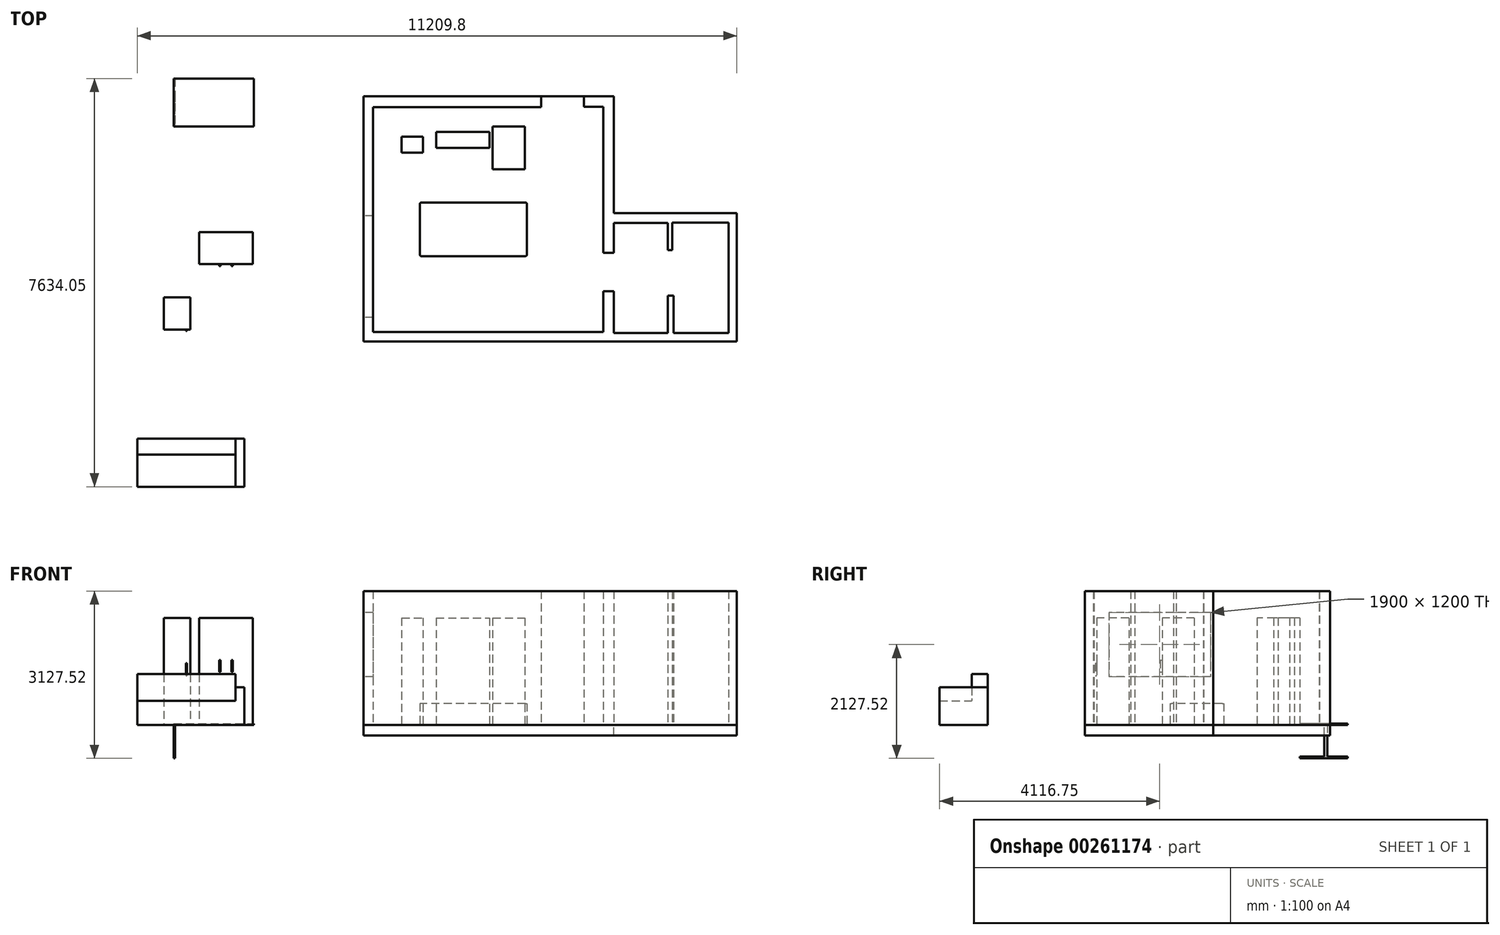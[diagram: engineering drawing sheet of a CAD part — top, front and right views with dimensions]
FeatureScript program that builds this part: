
annotation { "Feature Type Name" : "Feature", "Feature Type Description" : "" }
export const myFeature = defineFeature(function(context is Context, id is Id, definition is map)
    precondition{}
    {
        {
            var Q0;
            Q0=qCreatedBy(makeId("Top.planeOp"),FACE);
            var sketch = newSketch(context, id + "F0", { "sketchPlane" : qUnion([Q0])});
            skLineSegment(sketch, "E0", {"start": v(-190.9, 2081.06) * mm, "end": v(-3330.86, 2081.06) * mm});
            skLineSegment(sketch, "E1", {"start": v(-3330.86, 2081.06) * mm, "end": v(-3330.86, -2128.66) * mm});
            skLineSegment(sketch, "E2", {"start": v(-3330.86, -2128.66) * mm, "end": v(971.2, -2128.66) * mm});
            skLineSegment(sketch, "E3", {"start": v(971.2, -2128.66) * mm, "end": v(971.2, -1366.75) * mm});
            skLineSegment(sketch, "E4", {"start": v(971.2, -1366.75) * mm, "end": v(1171.3, -1366.75) * mm});
            skLineSegment(sketch, "E5", {"start": v(1171.3, -1366.75) * mm, "end": v(1171.3, -2144.05) * mm});
            skLineSegment(sketch, "E6", {"start": v(1171.3, -2144.05) * mm, "end": v(2179.48, -2144.05) * mm});
            skLineSegment(sketch, "E7", {"start": v(2179.48, -2144.05) * mm, "end": v(2179.48, -1443.71) * mm});
            skLineSegment(sketch, "E8", {"start": v(2179.48, -1443.71) * mm, "end": v(2287.22, -1443.71) * mm});
            skLineSegment(sketch, "E9", {"start": v(2287.22, -1443.71) * mm, "end": v(2287.22, -2144.05) * mm});
            skLineSegment(sketch, "E10", {"start": v(2287.22, -2144.05) * mm, "end": v(3318.49, -2144.05) * mm});
            skLineSegment(sketch, "E11", {"start": v(3318.49, -2144.05) * mm, "end": v(3318.49, -81.52) * mm});
            skLineSegment(sketch, "E12", {"start": v(3318.49, -81.52) * mm, "end": v(2264.13, -81.52) * mm});
            skLineSegment(sketch, "E13", {"start": v(2264.13, -81.52) * mm, "end": v(2264.13, -597.15) * mm});
            skLineSegment(sketch, "E14", {"start": v(2264.13, -597.15) * mm, "end": v(2179.48, -597.15) * mm});
            skLineSegment(sketch, "E15", {"start": v(2179.48, -597.15) * mm, "end": v(2179.48, -89.22) * mm});
            skLineSegment(sketch, "E16", {"start": v(2179.48, -89.22) * mm, "end": v(1171.3, -89.22) * mm});
            skLineSegment(sketch, "E17", {"start": v(1171.3, -89.22) * mm, "end": v(1171.3, -644.92) * mm});
            skLineSegment(sketch, "E18", {"start": v(1171.3, -644.92) * mm, "end": v(971.2, -644.92) * mm});
            skLineSegment(sketch, "E19", {"start": v(971.2, -644.92) * mm, "end": v(971.2, 2085.36) * mm});
            skLineSegment(sketch, "E20", {"start": v(971.2, 2085.36) * mm, "end": v(609.1, 2085.36) * mm});
            skLineSegment(sketch, "E21", {"start": v(609.1, 2085.36) * mm, "end": v(609.1, 2284.04) * mm});
            skLineSegment(sketch, "E22", {"start": v(609.1, 2284.04) * mm, "end": v(1171.3, 2284.04) * mm});
            skLineSegment(sketch, "E23", {"start": v(1171.3, 2284.04) * mm, "end": v(1171.3, 98.5) * mm});
            skLineSegment(sketch, "E24", {"start": v(1171.3, 98.5) * mm, "end": v(3468.44, 98.5) * mm});
            skLineSegment(sketch, "E25", {"start": v(3468.44, 98.5) * mm, "end": v(3468.44, -2303) * mm});
            skLineSegment(sketch, "E26", {"start": v(3468.44, -2303) * mm, "end": v(-3511.44, -2303) * mm});
            skLineSegment(sketch, "E27", {"start": v(-190.9, 2081.06) * mm, "end": v(-190.9, 2284.04) * mm});
            skLineSegment(sketch, "E28", {"start": v(-190.9, 2284.04) * mm, "end": v(-3511.44, 2284.04) * mm});
            skLineSegment(sketch, "E29", {"start": v(-3511.44, 2284.04) * mm, "end": v(-3511.44, -2303) * mm});
            skSolve(sketch);
        }
        {
            var Q0;
            Q0=qCreatedBy(makeId("Top.planeOp"),FACE);
            var sketch = newSketch(context, id + "F1", { "sketchPlane" : qUnion([Q0])});
            skLineSegment(sketch, "E30.bottom", {"start": v(-1094.62, 1714.75) * mm, "end": v(-494.62, 1714.75) * mm});
            skLineSegment(sketch, "E30.top", {"start": v(-1094.62, 914.75) * mm, "end": v(-494.62, 914.75) * mm});
            skLineSegment(sketch, "E30.left", {"start": v(-1094.62, 1714.75) * mm, "end": v(-1094.62, 914.75) * mm});
            skLineSegment(sketch, "E30.right", {"start": v(-494.62, 1714.75) * mm, "end": v(-494.62, 914.75) * mm});
            skSolve(sketch);
        }
        {
            var Q0;
            Q0 = qSketchRegion(id + "F0", true);
            extrude(context, id + "F2", {"entities" : qUnion([Q0]), "depth" : 2500 * mm});
        }
        {
            var Q0;
            Q0=makeQuery(id+"F2.opExtrude","SWEPT_FACE",FACE,{"disambiguationData":[OSD([sQuery(id+"F0.wireOp",EDGE,"E29")])]});
            var sketch = newSketch(context, id + "F3", { "sketchPlane" : qUnion([Q0])});
            skLineSegment(sketch, "E31.bottom", {"start": v(-47, 2100) * mm, "end": v(1853, 2100) * mm});
            skLineSegment(sketch, "E31.top", {"start": v(-47, 900) * mm, "end": v(1853, 900) * mm});
            skLineSegment(sketch, "E31.left", {"start": v(-47, 2100) * mm, "end": v(-47, 900) * mm});
            skLineSegment(sketch, "E31.right", {"start": v(1853, 2100) * mm, "end": v(1853, 900) * mm});
            skSolve(sketch);
        }
        {
            var Q0;
            Q0 = qSketchRegion(id + "F3", true);
            extrude(context, id + "F4", {"entities" : qUnion([Q0]), "operationType" : NewBodyOperationType.REMOVE, "endBound" : BoundingType.UP_TO_NEXT, "oppositeDirection" : true, "depth" : 25 * mm});
        }
        {
            var Q0;
            Q0=makeQuery(id+"F1.imprint","IMPRINT",FACE,{"disambiguationData":[TD([[makeQuery(id+"F1.imprint","IMPRINT",EDGE,{"derivedFrom":sQuery(id+"F1.wireOp",EDGE,"E30.bottom")}),-1.0]])]});
            extrude(context, id + "F5", {"entities" : qUnion([Q0]), "depth" : 2000 * mm});
        }
        {
            var Q0;
            Q0=qCreatedBy(makeId("Top.planeOp"),FACE);
            var sketch = newSketch(context, id + "F6", { "sketchPlane" : qUnion([Q0])});
            skLineSegment(sketch, "E32.bottom", {"start": v(-481.22, 293.15) * mm, "end": v(-2431.22, 293.15) * mm});
            skLineSegment(sketch, "E32.top", {"start": v(-481.22, -706.85) * mm, "end": v(-2431.22, -706.85) * mm});
            skLineSegment(sketch, "E32.left", {"start": v(-456.22, 268.15) * mm, "end": v(-456.22, -681.85) * mm});
            skLineSegment(sketch, "E32.right", {"start": v(-2456.22, 268.15) * mm, "end": v(-2456.22, -681.85) * mm});
            skPoint(sketch, "E33.visualSharp", {"position": v(-2456.22, -706.85) * mm});
            skArc(sketch, "E33.filletArc", {"start": v(-2456.22, -681.85) * mm, "mid": v(-2448.9, -699.53) * mm, "end": v(-2431.22, -706.85) * mm});
            skPoint(sketch, "E34.visualSharp", {"position": v(-456.22, -706.85) * mm});
            skArc(sketch, "E34.filletArc", {"start": v(-481.22, -706.85) * mm, "mid": v(-463.54, -699.53) * mm, "end": v(-456.22, -681.85) * mm});
            skPoint(sketch, "E35.visualSharp", {"position": v(-456.22, 293.15) * mm});
            skArc(sketch, "E35.filletArc", {"start": v(-456.22, 268.15) * mm, "mid": v(-463.54, 285.82) * mm, "end": v(-481.22, 293.15) * mm});
            skPoint(sketch, "E36.visualSharp", {"position": v(-2456.22, 293.15) * mm});
            skArc(sketch, "E36.filletArc", {"start": v(-2431.22, 293.15) * mm, "mid": v(-2448.9, 285.82) * mm, "end": v(-2456.22, 268.15) * mm});
            skSolve(sketch);
        }
        {
            var Q0;
            Q0 = qSketchRegion(id + "F6", true);
            extrude(context, id + "F7", {"entities" : qUnion([Q0]), "depth" : 400 * mm});
        }
        {
            var Q0;
            Q0=qCreatedBy(makeId("Top.planeOp"),FACE);
            var sketch = newSketch(context, id + "F8", { "sketchPlane" : qUnion([Q0])});
            skLineSegment(sketch, "E37.bottom", {"start": v(-2799.21, 1526.86) * mm, "end": v(-2399.21, 1526.86) * mm});
            skLineSegment(sketch, "E37.top", {"start": v(-2799.21, 1226.86) * mm, "end": v(-2399.21, 1226.86) * mm});
            skLineSegment(sketch, "E37.left", {"start": v(-2799.21, 1526.86) * mm, "end": v(-2799.21, 1226.86) * mm});
            skLineSegment(sketch, "E37.right", {"start": v(-2399.21, 1526.86) * mm, "end": v(-2399.21, 1226.86) * mm});
            skSolve(sketch);
        }
        {
            var Q0;
            Q0 = qSketchRegion(id + "F8", true);
            extrude(context, id + "F9", {"entities" : qUnion([Q0]), "depth" : 2000 * mm});
        }
        {
            var Q0;
            Q0=qCreatedBy(makeId("Top.planeOp"),FACE);
            var sketch = newSketch(context, id + "F10", { "sketchPlane" : qUnion([Q0])});
            skLineSegment(sketch, "E38.bottom", {"start": v(-2154.1, 1613.02) * mm, "end": v(-1154.1, 1613.02) * mm});
            skLineSegment(sketch, "E38.top", {"start": v(-2154.1, 1313.02) * mm, "end": v(-1154.1, 1313.02) * mm});
            skLineSegment(sketch, "E38.left", {"start": v(-2154.1, 1613.02) * mm, "end": v(-2154.1, 1313.02) * mm});
            skLineSegment(sketch, "E38.right", {"start": v(-1154.1, 1613.02) * mm, "end": v(-1154.1, 1313.02) * mm});
            skSolve(sketch);
        }
        {
            var Q0;
            Q0 = qSketchRegion(id + "F10", true);
            extrude(context, id + "F11", {"entities" : qUnion([Q0]), "depth" : 2000 * mm});
        }
        {
            var Q0;
            Q0=makeQuery(id+"F2.opExtrude","CAP_FACE",FACE,{"disambiguationData":[OSD([sQuery(id+"F0.wireOp",EDGE,"E0"),sQuery(id+"F0.wireOp",EDGE,"E1"),sQuery(id+"F0.wireOp",EDGE,"E2"),sQuery(id+"F0.wireOp",EDGE,"E3"),sQuery(id+"F0.wireOp",EDGE,"E4"),sQuery(id+"F0.wireOp",EDGE,"E5"),sQuery(id+"F0.wireOp",EDGE,"E6"),sQuery(id+"F0.wireOp",EDGE,"E7"),sQuery(id+"F0.wireOp",EDGE,"E8"),sQuery(id+"F0.wireOp",EDGE,"E9"),sQuery(id+"F0.wireOp",EDGE,"E10"),sQuery(id+"F0.wireOp",EDGE,"E11"),sQuery(id+"F0.wireOp",EDGE,"E12"),sQuery(id+"F0.wireOp",EDGE,"E13"),sQuery(id+"F0.wireOp",EDGE,"E14"),sQuery(id+"F0.wireOp",EDGE,"E15"),sQuery(id+"F0.wireOp",EDGE,"E16"),sQuery(id+"F0.wireOp",EDGE,"E17"),sQuery(id+"F0.wireOp",EDGE,"E18"),sQuery(id+"F0.wireOp",EDGE,"E19"),sQuery(id+"F0.wireOp",EDGE,"E20"),sQuery(id+"F0.wireOp",EDGE,"E21"),sQuery(id+"F0.wireOp",EDGE,"E22"),sQuery(id+"F0.wireOp",EDGE,"E23"),sQuery(id+"F0.wireOp",EDGE,"E24"),sQuery(id+"F0.wireOp",EDGE,"E25"),sQuery(id+"F0.wireOp",EDGE,"E26"),sQuery(id+"F0.wireOp",EDGE,"E27"),sQuery(id+"F0.wireOp",EDGE,"E28"),sQuery(id+"F0.wireOp",EDGE,"E29")])],"isStart":true});
            var sketch = newSketch(context, id + "F12", { "sketchPlane" : qUnion([Q0])});
            skLineSegment(sketch, "E39", {"start": v(-3511.44, 2303) * mm, "end": v(3468.44, 2303) * mm});
            skLineSegment(sketch, "E40", {"start": v(3468.44, 2303) * mm, "end": v(3468.44, -98.5) * mm});
            skLineSegment(sketch, "E41", {"start": v(3468.44, -98.5) * mm, "end": v(1171.3, -98.5) * mm});
            skLineSegment(sketch, "E42", {"start": v(1171.3, -98.5) * mm, "end": v(1171.3, -2284.04) * mm});
            skLineSegment(sketch, "E43", {"start": v(1171.3, -2284.04) * mm, "end": v(-3511.44, -2284.04) * mm});
            skLineSegment(sketch, "E44", {"start": v(-3511.44, -2284.04) * mm, "end": v(-3511.44, 2303) * mm});
            skSolve(sketch);
        }
        {
            var Q0;
            Q0 = qSketchRegion(id + "F12", true);
            extrude(context, id + "F13", {"entities" : qUnion([Q0]), "depth" : 200 * mm});
        }
        {
            var Q0;
            Q0=qCreatedBy(makeId("Top.planeOp"),FACE);
            var sketch = newSketch(context, id + "F14", { "sketchPlane" : qUnion([Q0])});
            skLineSegment(sketch, "E45.bottom", {"start": v(-7060.45, 2614.3) * mm, "end": v(-5560.45, 2614.3) * mm});
            skLineSegment(sketch, "E45.top", {"start": v(-7060.45, 1714.3) * mm, "end": v(-5560.45, 1714.3) * mm});
            skLineSegment(sketch, "E45.left", {"start": v(-7060.45, 2614.3) * mm, "end": v(-7060.45, 1714.3) * mm});
            skLineSegment(sketch, "E45.right", {"start": v(-5560.45, 2614.3) * mm, "end": v(-5560.45, 1714.3) * mm});
            skSolve(sketch);
        }
        {
            var Q0;
            Q0 = qSketchRegion(id + "F14", true);
            extrude(context, id + "F15", {"entities" : qUnion([Q0]), "depth" : 20 * mm});
        }
        {
            var Q0;
            Q0=makeQuery(id+"F15.opExtrude","SWEPT_FACE",FACE,{"disambiguationData":[OSD([sQuery(id+"F14.wireOp",EDGE,"E45.left")])]});
            var sketch = newSketch(context, id + "F16", { "sketchPlane" : qUnion([Q0])});
            skLineSegment(sketch, "E46", {"start": v(-2228.83, 0) * mm, "end": v(-2228.83, -593.03) * mm});
            skLineSegment(sketch, "E47", {"start": v(-2228.83, -593.03) * mm, "end": v(-2614.3, -593.03) * mm});
            skLineSegment(sketch, "E48", {"start": v(-2614.3, -593.03) * mm, "end": v(-2614.3, -627.52) * mm});
            skLineSegment(sketch, "E49", {"start": v(-2614.3, -627.52) * mm, "end": v(-1714.3, -627.52) * mm});
            skLineSegment(sketch, "E50", {"start": v(-1714.3, -627.52) * mm, "end": v(-1714.3, -593.03) * mm});
            skLineSegment(sketch, "E51", {"start": v(-1714.3, -593.03) * mm, "end": v(-2176.35, -593.03) * mm});
            skLineSegment(sketch, "E52", {"start": v(-2176.35, -593.03) * mm, "end": v(-2176.35, 0) * mm});
            skLineSegment(sketch, "E53", {"start": v(-2176.35, 0) * mm, "end": v(-2228.83, 0) * mm});
            skSolve(sketch);
        }
        {
            var Q0;
            Q0 = qSketchRegion(id + "F16", true);
            extrude(context, id + "F17", {"entities" : qUnion([Q0]), "oppositeDirection" : true, "depth" : 25 * mm});
        }
        {
            var Q0;
            Q0=qCreatedBy(makeId("Top.planeOp"),FACE);
            var sketch = newSketch(context, id + "F18", { "sketchPlane" : qUnion([Q0])});
            skLineSegment(sketch, "E54.bottom", {"start": v(-6581.38, -256.22) * mm, "end": v(-5581.38, -256.22) * mm});
            skLineSegment(sketch, "E54.top", {"start": v(-6581.38, -856.22) * mm, "end": v(-5581.38, -856.22) * mm});
            skLineSegment(sketch, "E54.left", {"start": v(-6581.38, -256.22) * mm, "end": v(-6581.38, -856.22) * mm});
            skLineSegment(sketch, "E54.right", {"start": v(-5581.38, -256.22) * mm, "end": v(-5581.38, -856.22) * mm});
            skSolve(sketch);
        }
        {
            var Q0;
            Q0=qCreatedBy(makeId("Top.planeOp"),FACE);
            var sketch = newSketch(context, id + "F19", { "sketchPlane" : qUnion([Q0])});
            skLineSegment(sketch, "E55.bottom", {"start": v(-7247.05, -1478.38) * mm, "end": v(-6747.05, -1478.38) * mm});
            skLineSegment(sketch, "E55.top", {"start": v(-7247.05, -2078.38) * mm, "end": v(-6747.05, -2078.38) * mm});
            skLineSegment(sketch, "E55.left", {"start": v(-7247.05, -1478.38) * mm, "end": v(-7247.05, -2078.38) * mm});
            skLineSegment(sketch, "E55.right", {"start": v(-6747.05, -1478.38) * mm, "end": v(-6747.05, -2078.38) * mm});
            skSolve(sketch);
        }
        {
            var Q0;
            Q0=makeQuery(id+"F19.imprint","IMPRINT",FACE,{"disambiguationData":[TD([[makeQuery(id+"F19.imprint","IMPRINT",EDGE,{"derivedFrom":sQuery(id+"F19.wireOp",EDGE,"E55.bottom")}),-1.0]])]});
            extrude(context, id + "F20", {"entities" : qUnion([Q0]), "depth" : 2000 * mm});
        }
        {
            var Q0;
            Q0=makeQuery(id+"F18.imprint","IMPRINT",FACE,{"disambiguationData":[TD([[makeQuery(id+"F18.imprint","IMPRINT",EDGE,{"derivedFrom":sQuery(id+"F18.wireOp",EDGE,"E54.bottom")}),-1.0]])]});
            extrude(context, id + "F21", {"entities" : qUnion([Q0]), "depth" : 2000 * mm});
        }
        {
            var Q0;
            Q0=makeQuery(id+"F21.opExtrude","SWEPT_FACE",FACE,{"disambiguationData":[OSD([sQuery(id+"F18.wireOp",EDGE,"E54.top")])]});
            var sketch = newSketch(context, id + "F22", { "sketchPlane" : qUnion([Q0])});
            skLineSegment(sketch, "E56.bottom", {"start": v(-6206.1, 1210.76) * mm, "end": v(-6183.06, 1210.76) * mm});
            skLineSegment(sketch, "E56.top", {"start": v(-6206.1, 990.48) * mm, "end": v(-6183.06, 990.48) * mm});
            skLineSegment(sketch, "E56.left", {"start": v(-6206.1, 1210.76) * mm, "end": v(-6206.1, 990.48) * mm});
            skLineSegment(sketch, "E56.right", {"start": v(-6183.06, 1210.76) * mm, "end": v(-6183.06, 990.48) * mm});
            skLineSegment(sketch, "E57", {"start": v(-6081.38, 2000) * mm, "end": v(-6081.38, 0) * mm, "construction": true});
            skLineSegment(sketch, "E58.MirrorCS", {"start": v(-5979.7, 1210.76) * mm, "end": v(-5979.7, 990.48) * mm});
            skLineSegment(sketch, "E59.MirrorCS", {"start": v(-5956.65, 1210.76) * mm, "end": v(-5956.65, 990.48) * mm});
            skLineSegment(sketch, "E60.MirrorCS", {"start": v(-5956.65, 990.48) * mm, "end": v(-5979.7, 990.48) * mm});
            skLineSegment(sketch, "E61.MirrorCS", {"start": v(-5956.65, 1210.76) * mm, "end": v(-5979.7, 1210.76) * mm});
            skSolve(sketch);
        }
        {
            var Q0;
            Q0=makeQuery(id+"F22.imprint","IMPRINT",FACE,{"disambiguationData":[TD([[makeQuery(id+"F22.imprint","IMPRINT",EDGE,{"derivedFrom":sQuery(id+"F22.wireOp",EDGE,"E56.bottom")}),-1.0]])]});
            var Q1;
            Q1=makeQuery(id+"F22.imprint","IMPRINT",FACE,{"disambiguationData":[TD([[makeQuery(id+"F22.imprint","IMPRINT",EDGE,{"derivedFrom":sQuery(id+"F22.wireOp",EDGE,"E58.MirrorCS")}),1.0]])]});
            extrude(context, id + "F23", {"entities" : qUnion([Q0, Q1]), "operationType" : NewBodyOperationType.ADD, "depth" : 37 * mm});
        }
        {
            var Q0;
            Q0=makeQuery(id+"F20.opExtrude","SWEPT_FACE",FACE,{"disambiguationData":[OSD([sQuery(id+"F19.wireOp",EDGE,"E55.top")])]});
            var sketch = newSketch(context, id + "F24", { "sketchPlane" : qUnion([Q0])});
            skLineSegment(sketch, "E62.bottom", {"start": v(-6833.46, 1150.72) * mm, "end": v(-6811.29, 1150.72) * mm});
            skLineSegment(sketch, "E62.top", {"start": v(-6833.46, 918.65) * mm, "end": v(-6811.29, 918.65) * mm});
            skLineSegment(sketch, "E62.left", {"start": v(-6833.46, 1150.72) * mm, "end": v(-6833.46, 918.65) * mm});
            skLineSegment(sketch, "E62.right", {"start": v(-6811.29, 1150.72) * mm, "end": v(-6811.29, 918.65) * mm});
            skSolve(sketch);
        }
        {
            var Q0;
            Q0=makeQuery(id+"F24.imprint","IMPRINT",FACE,{"disambiguationData":[TD([[makeQuery(id+"F24.imprint","IMPRINT",EDGE,{"derivedFrom":sQuery(id+"F24.wireOp",EDGE,"E62.bottom")}),-1.0]])]});
            extrude(context, id + "F25", {"entities" : qUnion([Q0]), "operationType" : NewBodyOperationType.ADD, "depth" : 30 * mm});
        }
        {
            var Q0;
            Q0=qCreatedBy(makeId("Top.planeOp"),FACE);
            var sketch = newSketch(context, id + "F26", { "sketchPlane" : qUnion([Q0])});
            skLineSegment(sketch, "E63.bottom", {"start": v(-7741.32, -4119.74) * mm, "end": v(-5741.32, -4119.74) * mm});
            skLineSegment(sketch, "E63.top", {"start": v(-7741.32, -5019.74) * mm, "end": v(-5741.32, -5019.74) * mm});
            skLineSegment(sketch, "E63.left", {"start": v(-7741.32, -4119.74) * mm, "end": v(-7741.32, -5019.74) * mm});
            skLineSegment(sketch, "E63.right", {"start": v(-5741.32, -4119.74) * mm, "end": v(-5741.32, -5019.74) * mm});
            skSolve(sketch);
        }
        {
            var Q0;
            Q0=makeQuery(id+"F26.imprint","IMPRINT",FACE,{"disambiguationData":[TD([[makeQuery(id+"F26.imprint","IMPRINT",EDGE,{"derivedFrom":sQuery(id+"F26.wireOp",EDGE,"E63.bottom")}),-1.0]])]});
            extrude(context, id + "F27", {"entities" : qUnion([Q0]), "depth" : 450 * mm});
        }
        {
            var Q0;
            Q0=makeQuery(id+"F27.opExtrude","CAP_FACE",FACE,{"disambiguationData":[OSD([sQuery(id+"F26.wireOp",EDGE,"E63.bottom"),sQuery(id+"F26.wireOp",EDGE,"E63.top"),sQuery(id+"F26.wireOp",EDGE,"E63.left"),sQuery(id+"F26.wireOp",EDGE,"E63.right")])],"isStart":false});
            var sketch = newSketch(context, id + "F28", { "sketchPlane" : qUnion([Q0])});
            skLineSegment(sketch, "E64", {"start": v(-7741.32, -4119.74) * mm, "end": v(-7741.32, -4419.74) * mm});
            skLineSegment(sketch, "E65", {"start": v(-7741.32, -4419.74) * mm, "end": v(-5906.64, -4419.74) * mm});
            skLineSegment(sketch, "E66", {"start": v(-5906.64, -4419.74) * mm, "end": v(-5906.64, -5019.74) * mm});
            skLineSegment(sketch, "E67", {"start": v(-5906.64, -5019.74) * mm, "end": v(-5741.32, -5019.74) * mm});
            skLineSegment(sketch, "E68", {"start": v(-5741.32, -5019.74) * mm, "end": v(-5741.32, -4119.74) * mm});
            skLineSegment(sketch, "E69", {"start": v(-5741.32, -4119.74) * mm, "end": v(-7741.32, -4119.74) * mm});
            skLineSegment(sketch, "E70", {"start": v(-5906.64, -4419.74) * mm, "end": v(-5906.64, -4119.74) * mm});
            skSolve(sketch);
        }
        {
            var Q0;
            {var subQ0=sQuery(id+"F28.wireOp",EDGE,"E64");Q0=makeQuery(id+"F28.imprint","IMPRINT",FACE,{"disambiguationData":[TD([[makeQuery(id+"F28.imprint","IMPRINT",EDGE,{"derivedFrom":subQ0}),1.0]])]});}
            extrude(context, id + "F29", {"entities" : qUnion([Q0]), "operationType" : NewBodyOperationType.ADD, "depth" : 500 * mm});
        }
        {
            var Q0;
            Q0=makeQuery(id+"F27.opExtrude","CAP_FACE",FACE,{"disambiguationData":[OSD([sQuery(id+"F26.wireOp",EDGE,"E63.bottom"),sQuery(id+"F26.wireOp",EDGE,"E63.top"),sQuery(id+"F26.wireOp",EDGE,"E63.left"),sQuery(id+"F26.wireOp",EDGE,"E63.right")])],"isStart":false});
            var sketch = newSketch(context, id + "F30", { "sketchPlane" : qUnion([Q0])});
            skLineSegment(sketch, "E71.bottom", {"start": v(-5906.64, -4119.74) * mm, "end": v(-5741.32, -4119.74) * mm});
            skLineSegment(sketch, "E71.top", {"start": v(-5906.64, -5019.74) * mm, "end": v(-5741.32, -5019.74) * mm});
            skLineSegment(sketch, "E71.left", {"start": v(-5906.64, -4119.74) * mm, "end": v(-5906.64, -5019.74) * mm});
            skLineSegment(sketch, "E71.right", {"start": v(-5741.32, -4119.74) * mm, "end": v(-5741.32, -5019.74) * mm});
            skSolve(sketch);
        }
        {
            var Q0;
            {var subQ2=sQuery(id+"F30.wireOp",EDGE,"E71.bottom");Q0=makeQuery(id+"F30.imprint","IMPRINT",FACE,{"disambiguationData":[TD([[makeQuery(id+"F30.imprint","IMPRINT",EDGE,{"derivedFrom":subQ2}),-1.0]])]});}
            extrude(context, id + "F31", {"entities" : qUnion([Q0]), "operationType" : NewBodyOperationType.ADD, "depth" : 250 * mm});
        }
    });
